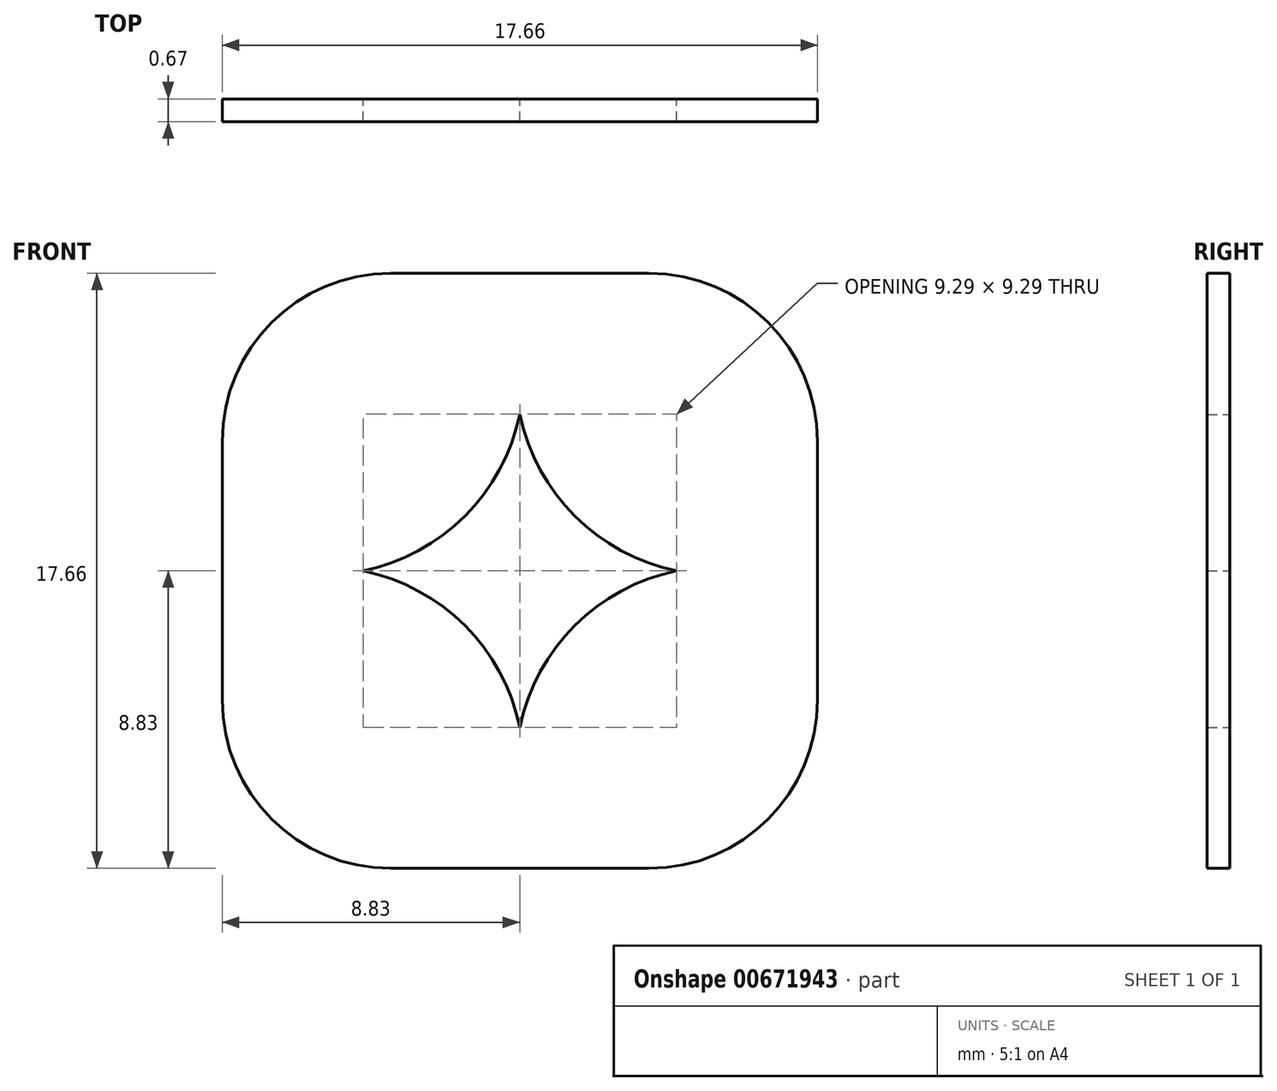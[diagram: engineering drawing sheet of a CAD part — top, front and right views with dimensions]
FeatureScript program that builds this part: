
annotation { "Feature Type Name" : "Feature", "Feature Type Description" : "" }
export const myFeature = defineFeature(function(context is Context, id is Id, definition is map)
    precondition{}
    {
        {
            var Q0;
            Q0=qCreatedBy(makeId("Front.planeOp"),FACE);
            var sketch = newSketch(context, id + "F0", { "sketchPlane" : qUnion([Q0])});
            skLineSegment(sketch, "E0.bottom", {"start": v(-3.83, 8.83) * mm, "end": v(3.83, 8.83) * mm});
            skLineSegment(sketch, "E0.top", {"start": v(-3.83, -8.83) * mm, "end": v(3.83, -8.83) * mm});
            skLineSegment(sketch, "E0.left", {"start": v(-8.83, 3.83) * mm, "end": v(-8.83, -3.83) * mm});
            skLineSegment(sketch, "E0.right", {"start": v(8.83, 3.83) * mm, "end": v(8.83, -3.83) * mm});
            skPoint(sketch, "E0.middle", {"position": v(0, 0) * mm});
            skArc(sketch, "E1", {"start": v(0, -4.64) * mm, "mid": v(-1.63, -1.63) * mm, "end": v(-4.64, 0) * mm});
            skArc(sketch, "E2", {"start": v(4.64, 0) * mm, "mid": v(1.63, -1.63) * mm, "end": v(0, -4.64) * mm});
            skArc(sketch, "E3", {"start": v(0, 4.64) * mm, "mid": v(1.63, 1.63) * mm, "end": v(4.64, 0) * mm});
            skArc(sketch, "E4", {"start": v(-4.64, 0) * mm, "mid": v(-1.63, 1.63) * mm, "end": v(0, 4.64) * mm});
            skPoint(sketch, "E5.visualSharp", {"position": v(-8.83, 8.83) * mm});
            skArc(sketch, "E5.filletArc", {"start": v(-3.83, 8.83) * mm, "mid": v(-7.37, 7.37) * mm, "end": v(-8.83, 3.83) * mm});
            skPoint(sketch, "E6.visualSharp", {"position": v(8.83, 8.83) * mm});
            skArc(sketch, "E6.filletArc", {"start": v(8.83, 3.83) * mm, "mid": v(7.37, 7.37) * mm, "end": v(3.83, 8.83) * mm});
            skPoint(sketch, "E7.visualSharp", {"position": v(8.83, -8.83) * mm});
            skArc(sketch, "E7.filletArc", {"start": v(3.83, -8.83) * mm, "mid": v(7.37, -7.37) * mm, "end": v(8.83, -3.83) * mm});
            skPoint(sketch, "E8.visualSharp", {"position": v(-8.83, -8.83) * mm});
            skArc(sketch, "E8.filletArc", {"start": v(-8.83, -3.83) * mm, "mid": v(-7.37, -7.37) * mm, "end": v(-3.83, -8.83) * mm});
            skSolve(sketch);
        }
        {
            var Q0;
            Q0=makeQuery(id+"F0.imprint","IMPRINT",FACE,{"disambiguationData":[TD([[makeQuery(id+"F0.imprint","IMPRINT",EDGE,{"derivedFrom":sQuery(id+"F0.wireOp",EDGE,"E0.bottom")}),-1.0]])]});
            extrude(context, id + "F1", {"entities" : qUnion([Q0]), "depth" : 0.67 * mm, "offsetDistance" : 25 * mm});
        }
    });
